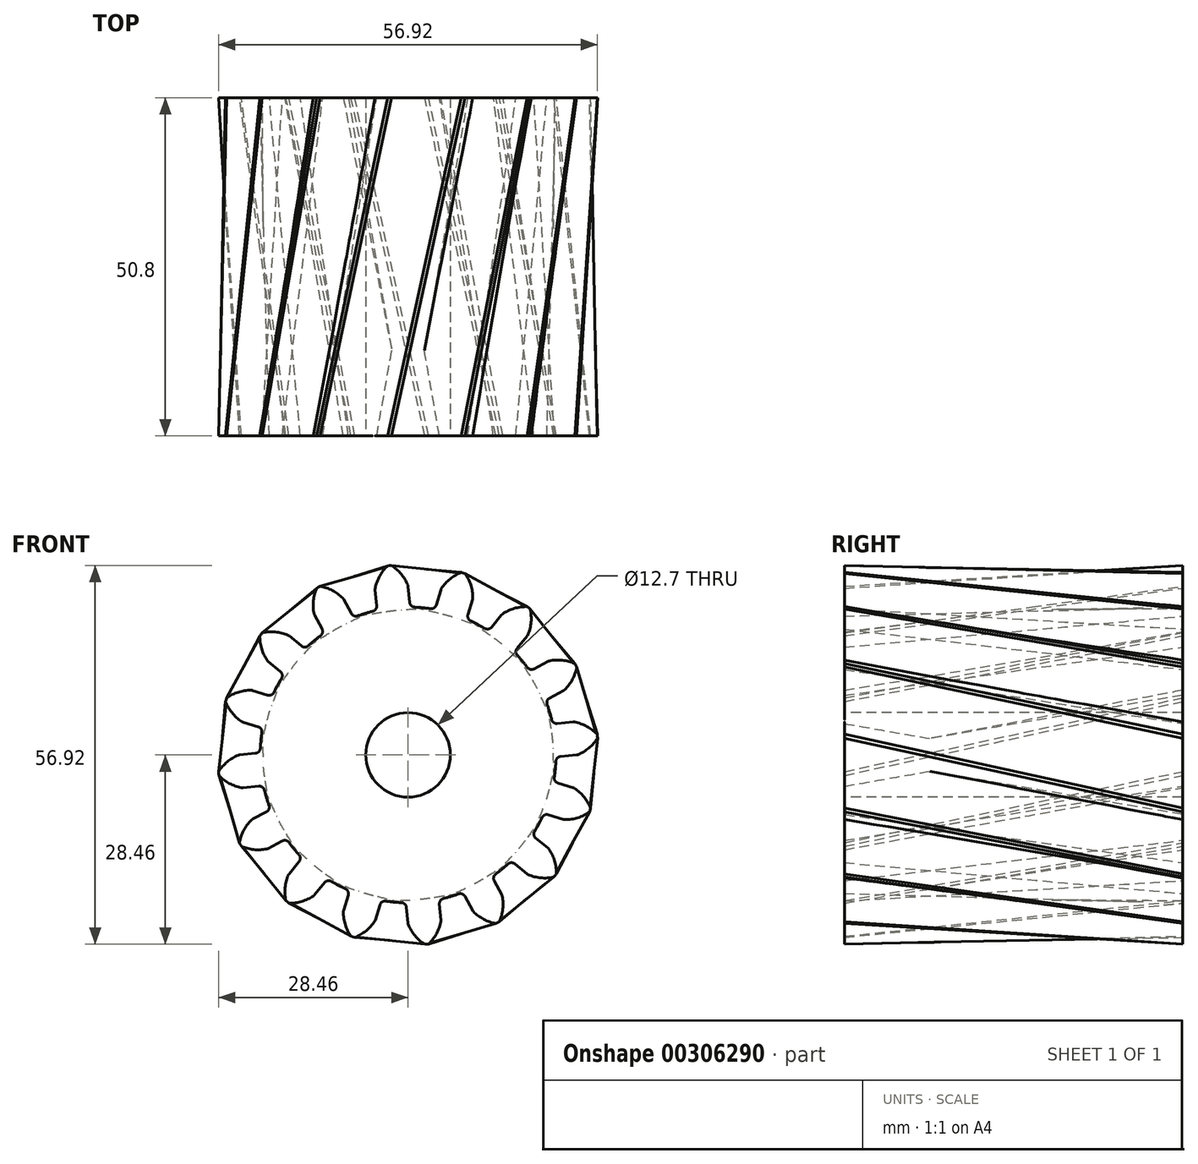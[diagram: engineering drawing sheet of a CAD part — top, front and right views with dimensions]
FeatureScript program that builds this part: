
annotation { "Feature Type Name" : "Feature", "Feature Type Description" : "" }
export const myFeature = defineFeature(function(context is Context, id is Id, definition is map)
    precondition{}
    {
        {
            var Q0;
            Q0=qCreatedBy(makeId("Front.planeOp"),FACE);
            var sketch = newSketch(context, id + "F0", { "sketchPlane" : qUnion([Q0])});
            skArc(sketch, "E0", {"start": v(-5.3, 21.58) * mm, "mid": v(-6.45, 21.27) * mm, "end": v(-7.58, 20.9) * mm});
            skArc(sketch, "E1.trimOffspring", {"start": v(-0.04, 25.51) * mm, "mid": v(-1.05, 27.18) * mm, "end": v(-2.5, 28.46) * mm});
            skLineSegment(sketch, "E2", {"start": v(-2.5, 28.46) * mm, "end": v(-2.8, 28.44) * mm});
            skLineSegment(sketch, "E3", {"start": v(0.01, 25.29) * mm, "end": v(0.25, 22.91) * mm});
            skLineSegment(sketch, "E4.MirrorCS", {"start": v(-3.1, 28.4) * mm, "end": v(-2.8, 28.44) * mm});
            skArc(sketch, "E5.MirrorCS", {"start": v(-4.93, 25.03) * mm, "mid": v(-4.28, 26.86) * mm, "end": v(-3.1, 28.4) * mm});
            skLineSegment(sketch, "E6.MirrorCS", {"start": v(-4.94, 24.8) * mm, "end": v(-4.71, 22.42) * mm});
            skPoint(sketch, "E7.orphan", {"position": v(-4.37, 19) * mm});
            skPoint(sketch, "E8.orphan", {"position": v(0.58, 19.48) * mm});
            skPoint(sketch, "E9.visualSharp", {"position": v(-4.96, 24.91) * mm});
            skArc(sketch, "E9.filletArc", {"start": v(-4.93, 25.03) * mm, "mid": v(-4.95, 24.92) * mm, "end": v(-4.94, 24.8) * mm});
            skPoint(sketch, "E10.visualSharp", {"position": v(0, 25.4) * mm});
            skArc(sketch, "E10.filletArc", {"start": v(0.01, 25.29) * mm, "mid": v(0, 25.4) * mm, "end": v(-0.04, 25.51) * mm});
            skPoint(sketch, "E11.visualSharp", {"position": v(0.31, 22.22) * mm});
            skArc(sketch, "E11.filletArc", {"start": v(0.25, 22.91) * mm, "mid": v(0.49, 22.42) * mm, "end": v(1, 22.2) * mm});
            skPoint(sketch, "E12.visualSharp", {"position": v(-4.64, 21.73) * mm});
            skArc(sketch, "E12.filletArc", {"start": v(-5.3, 21.58) * mm, "mid": v(-4.85, 21.9) * mm, "end": v(-4.71, 22.42) * mm});
            skArc(sketch, "E13.1.0", {"start": v(-14.14, 21.24) * mm, "mid": v(-14.23, 23.18) * mm, "end": v(-13.73, 25.06) * mm});
            skArc(sketch, "E13.1.1", {"start": v(-14.14, 21.24) * mm, "mid": v(-14.1, 21.13) * mm, "end": v(-14.06, 21.02) * mm});
            skLineSegment(sketch, "E13.1.2", {"start": v(-14.06, 21.02) * mm, "end": v(-12.93, 18.91) * mm});
            skArc(sketch, "E13.1.3", {"start": v(-9.67, 23.37) * mm, "mid": v(-9.73, 23.47) * mm, "end": v(-9.8, 23.55) * mm});
            skArc(sketch, "E13.1.4", {"start": v(-9.8, 23.55) * mm, "mid": v(-11.37, 24.7) * mm, "end": v(-13.21, 25.34) * mm});
            skLineSegment(sketch, "E13.1.5", {"start": v(-9.67, 23.37) * mm, "end": v(-8.54, 21.26) * mm});
            skLineSegment(sketch, "E13.1.6", {"start": v(-13.21, 25.34) * mm, "end": v(-13.47, 25.2) * mm});
            skLineSegment(sketch, "E13.1.7", {"start": v(-13.73, 25.06) * mm, "end": v(-13.47, 25.2) * mm});
            skArc(sketch, "E13.1.8", {"start": v(-13.16, 17.9) * mm, "mid": v(-12.86, 18.37) * mm, "end": v(-12.93, 18.91) * mm});
            skArc(sketch, "E13.1.9", {"start": v(-8.54, 21.26) * mm, "mid": v(-8.13, 20.9) * mm, "end": v(-7.58, 20.9) * mm});
            skArc(sketch, "E13.2.0", {"start": v(-21.19, 14.2) * mm, "mid": v(-22.02, 15.97) * mm, "end": v(-22.27, 17.9) * mm});
            skArc(sketch, "E13.2.1", {"start": v(-21.19, 14.2) * mm, "mid": v(-21.12, 14.12) * mm, "end": v(-21.03, 14.04) * mm});
            skLineSegment(sketch, "E13.2.2", {"start": v(-21.03, 14.04) * mm, "end": v(-19.19, 12.53) * mm});
            skArc(sketch, "E13.2.3", {"start": v(-17.87, 17.9) * mm, "mid": v(-17.97, 17.96) * mm, "end": v(-18.07, 18) * mm});
            skArc(sketch, "E13.2.4", {"start": v(-18.07, 18) * mm, "mid": v(-19.96, 18.48) * mm, "end": v(-21.9, 18.35) * mm});
            skLineSegment(sketch, "E13.2.5", {"start": v(-17.87, 17.9) * mm, "end": v(-16.03, 16.37) * mm});
            skLineSegment(sketch, "E13.2.6", {"start": v(-21.9, 18.35) * mm, "end": v(-22.09, 18.13) * mm});
            skLineSegment(sketch, "E13.2.7", {"start": v(-22.27, 17.9) * mm, "end": v(-22.09, 18.13) * mm});
            skArc(sketch, "E13.2.8", {"start": v(-19.01, 11.5) * mm, "mid": v(-18.91, 12.05) * mm, "end": v(-19.19, 12.53) * mm});
            skArc(sketch, "E13.2.9", {"start": v(-16.03, 16.37) * mm, "mid": v(-15.5, 16.2) * mm, "end": v(-15, 16.4) * mm});
            skArc(sketch, "E14.2.3.0", {"start": v(-25.01, 5.02) * mm, "mid": v(-26.45, 6.33) * mm, "end": v(-27.43, 8.01) * mm});
            skArc(sketch, "E14.4.3.0", {"start": v(-25.01, 5.02) * mm, "mid": v(-24.91, 4.96) * mm, "end": v(-24.8, 4.92) * mm});
            skLineSegment(sketch, "E14.8.3.0", {"start": v(-24.8, 4.92) * mm, "end": v(-22.52, 4.23) * mm});
            skArc(sketch, "E14.11.3.0", {"start": v(-23.36, 9.69) * mm, "mid": v(-23.47, 9.71) * mm, "end": v(-23.58, 9.72) * mm});
            skArc(sketch, "E14.15.3.0", {"start": v(-23.58, 9.72) * mm, "mid": v(-25.51, 9.43) * mm, "end": v(-27.26, 8.58) * mm});
            skLineSegment(sketch, "E14.19.3.0", {"start": v(-23.36, 9.69) * mm, "end": v(-21.07, 9) * mm});
            skLineSegment(sketch, "E14.22.3.0", {"start": v(-27.26, 8.58) * mm, "end": v(-27.35, 8.3) * mm});
            skLineSegment(sketch, "E14.25.3.0", {"start": v(-27.43, 8.01) * mm, "end": v(-27.35, 8.3) * mm});
            skArc(sketch, "E14.28.3.0", {"start": v(-21.97, 3.36) * mm, "mid": v(-22.08, 3.9) * mm, "end": v(-22.52, 4.23) * mm});
            skArc(sketch, "E14.32.3.0", {"start": v(-21.07, 9) * mm, "mid": v(-20.53, 9.03) * mm, "end": v(-20.13, 9.41) * mm});
            skArc(sketch, "E14.2.4.0", {"start": v(-25.03, -4.93) * mm, "mid": v(-26.86, -4.28) * mm, "end": v(-28.4, -3.1) * mm});
            skArc(sketch, "E14.4.4.0", {"start": v(-25.03, -4.93) * mm, "mid": v(-24.92, -4.95) * mm, "end": v(-24.8, -4.94) * mm});
            skLineSegment(sketch, "E14.8.4.0", {"start": v(-24.8, -4.94) * mm, "end": v(-22.42, -4.71) * mm});
            skArc(sketch, "E14.11.4.0", {"start": v(-25.29, 0.01) * mm, "mid": v(-25.4, 0) * mm, "end": v(-25.51, -0.04) * mm});
            skArc(sketch, "E14.15.4.0", {"start": v(-25.51, -0.04) * mm, "mid": v(-27.18, -1.05) * mm, "end": v(-28.46, -2.5) * mm});
            skLineSegment(sketch, "E14.19.4.0", {"start": v(-25.29, 0.01) * mm, "end": v(-22.91, 0.25) * mm});
            skLineSegment(sketch, "E14.22.4.0", {"start": v(-28.46, -2.5) * mm, "end": v(-28.44, -2.8) * mm});
            skLineSegment(sketch, "E14.25.4.0", {"start": v(-28.4, -3.1) * mm, "end": v(-28.44, -2.8) * mm});
            skArc(sketch, "E14.28.4.0", {"start": v(-21.58, -5.3) * mm, "mid": v(-21.9, -4.85) * mm, "end": v(-22.42, -4.71) * mm});
            skArc(sketch, "E14.32.4.0", {"start": v(-22.91, 0.25) * mm, "mid": v(-22.42, 0.49) * mm, "end": v(-22.2, 1) * mm});
            skArc(sketch, "E14.2.5.0", {"start": v(-21.24, -14.14) * mm, "mid": v(-23.18, -14.23) * mm, "end": v(-25.06, -13.73) * mm});
            skArc(sketch, "E14.4.5.0", {"start": v(-21.24, -14.14) * mm, "mid": v(-21.13, -14.1) * mm, "end": v(-21.02, -14.06) * mm});
            skLineSegment(sketch, "E14.8.5.0", {"start": v(-21.02, -14.06) * mm, "end": v(-18.91, -12.93) * mm});
            skArc(sketch, "E14.11.5.0", {"start": v(-23.37, -9.67) * mm, "mid": v(-23.47, -9.73) * mm, "end": v(-23.55, -9.8) * mm});
            skArc(sketch, "E14.15.5.0", {"start": v(-23.55, -9.8) * mm, "mid": v(-24.7, -11.37) * mm, "end": v(-25.34, -13.21) * mm});
            skLineSegment(sketch, "E14.19.5.0", {"start": v(-23.37, -9.67) * mm, "end": v(-21.26, -8.54) * mm});
            skLineSegment(sketch, "E14.22.5.0", {"start": v(-25.34, -13.21) * mm, "end": v(-25.2, -13.47) * mm});
            skLineSegment(sketch, "E14.25.5.0", {"start": v(-25.06, -13.73) * mm, "end": v(-25.2, -13.47) * mm});
            skArc(sketch, "E14.28.5.0", {"start": v(-17.9, -13.16) * mm, "mid": v(-18.37, -12.86) * mm, "end": v(-18.91, -12.93) * mm});
            skArc(sketch, "E14.32.5.0", {"start": v(-21.26, -8.54) * mm, "mid": v(-20.9, -8.13) * mm, "end": v(-20.9, -7.58) * mm});
            skArc(sketch, "E14.2.6.0", {"start": v(-14.2, -21.19) * mm, "mid": v(-15.97, -22.02) * mm, "end": v(-17.9, -22.27) * mm});
            skArc(sketch, "E14.4.6.0", {"start": v(-14.2, -21.19) * mm, "mid": v(-14.12, -21.12) * mm, "end": v(-14.04, -21.03) * mm});
            skLineSegment(sketch, "E14.8.6.0", {"start": v(-14.04, -21.03) * mm, "end": v(-12.53, -19.19) * mm});
            skArc(sketch, "E14.11.6.0", {"start": v(-17.9, -17.87) * mm, "mid": v(-17.96, -17.97) * mm, "end": v(-18, -18.07) * mm});
            skArc(sketch, "E14.15.6.0", {"start": v(-18, -18.07) * mm, "mid": v(-18.48, -19.96) * mm, "end": v(-18.35, -21.9) * mm});
            skLineSegment(sketch, "E14.19.6.0", {"start": v(-17.9, -17.87) * mm, "end": v(-16.37, -16.03) * mm});
            skLineSegment(sketch, "E14.22.6.0", {"start": v(-18.35, -21.9) * mm, "end": v(-18.13, -22.09) * mm});
            skLineSegment(sketch, "E14.25.6.0", {"start": v(-17.9, -22.27) * mm, "end": v(-18.13, -22.09) * mm});
            skArc(sketch, "E14.28.6.0", {"start": v(-11.5, -19.01) * mm, "mid": v(-12.05, -18.91) * mm, "end": v(-12.53, -19.19) * mm});
            skArc(sketch, "E14.32.6.0", {"start": v(-16.37, -16.03) * mm, "mid": v(-16.2, -15.5) * mm, "end": v(-16.4, -15) * mm});
            skArc(sketch, "E14.2.7.0", {"start": v(-5.02, -25.01) * mm, "mid": v(-6.33, -26.45) * mm, "end": v(-8.01, -27.43) * mm});
            skArc(sketch, "E14.4.7.0", {"start": v(-5.02, -25.01) * mm, "mid": v(-4.96, -24.91) * mm, "end": v(-4.92, -24.8) * mm});
            skLineSegment(sketch, "E14.8.7.0", {"start": v(-4.92, -24.8) * mm, "end": v(-4.23, -22.52) * mm});
            skArc(sketch, "E14.11.7.0", {"start": v(-9.69, -23.36) * mm, "mid": v(-9.71, -23.47) * mm, "end": v(-9.72, -23.58) * mm});
            skArc(sketch, "E14.15.7.0", {"start": v(-9.72, -23.58) * mm, "mid": v(-9.43, -25.51) * mm, "end": v(-8.58, -27.26) * mm});
            skLineSegment(sketch, "E14.19.7.0", {"start": v(-9.69, -23.36) * mm, "end": v(-9, -21.07) * mm});
            skLineSegment(sketch, "E14.22.7.0", {"start": v(-8.58, -27.26) * mm, "end": v(-8.3, -27.35) * mm});
            skLineSegment(sketch, "E14.25.7.0", {"start": v(-8.01, -27.43) * mm, "end": v(-8.3, -27.35) * mm});
            skArc(sketch, "E14.28.7.0", {"start": v(-3.36, -21.97) * mm, "mid": v(-3.9, -22.08) * mm, "end": v(-4.23, -22.52) * mm});
            skArc(sketch, "E14.32.7.0", {"start": v(-9, -21.07) * mm, "mid": v(-9.03, -20.53) * mm, "end": v(-9.41, -20.13) * mm});
            skArc(sketch, "E14.2.8.0", {"start": v(4.93, -25.03) * mm, "mid": v(4.28, -26.86) * mm, "end": v(3.1, -28.4) * mm});
            skArc(sketch, "E14.4.8.0", {"start": v(4.93, -25.03) * mm, "mid": v(4.95, -24.92) * mm, "end": v(4.94, -24.8) * mm});
            skLineSegment(sketch, "E14.8.8.0", {"start": v(4.94, -24.8) * mm, "end": v(4.71, -22.42) * mm});
            skArc(sketch, "E14.11.8.0", {"start": v(-0.01, -25.29) * mm, "mid": v(0, -25.4) * mm, "end": v(0.04, -25.51) * mm});
            skArc(sketch, "E14.15.8.0", {"start": v(0.04, -25.51) * mm, "mid": v(1.05, -27.18) * mm, "end": v(2.5, -28.46) * mm});
            skLineSegment(sketch, "E14.19.8.0", {"start": v(-0.01, -25.29) * mm, "end": v(-0.25, -22.91) * mm});
            skLineSegment(sketch, "E14.22.8.0", {"start": v(2.5, -28.46) * mm, "end": v(2.8, -28.44) * mm});
            skLineSegment(sketch, "E14.25.8.0", {"start": v(3.1, -28.4) * mm, "end": v(2.8, -28.44) * mm});
            skArc(sketch, "E14.28.8.0", {"start": v(5.3, -21.58) * mm, "mid": v(4.85, -21.9) * mm, "end": v(4.71, -22.42) * mm});
            skArc(sketch, "E14.32.8.0", {"start": v(-0.25, -22.91) * mm, "mid": v(-0.49, -22.42) * mm, "end": v(-1, -22.2) * mm});
            skArc(sketch, "E14.2.9.0", {"start": v(14.14, -21.24) * mm, "mid": v(14.23, -23.18) * mm, "end": v(13.73, -25.06) * mm});
            skArc(sketch, "E14.4.9.0", {"start": v(14.14, -21.24) * mm, "mid": v(14.1, -21.13) * mm, "end": v(14.06, -21.02) * mm});
            skLineSegment(sketch, "E14.8.9.0", {"start": v(14.06, -21.02) * mm, "end": v(12.93, -18.91) * mm});
            skArc(sketch, "E14.11.9.0", {"start": v(9.67, -23.37) * mm, "mid": v(9.73, -23.47) * mm, "end": v(9.8, -23.55) * mm});
            skArc(sketch, "E14.15.9.0", {"start": v(9.8, -23.55) * mm, "mid": v(11.37, -24.7) * mm, "end": v(13.21, -25.34) * mm});
            skLineSegment(sketch, "E14.19.9.0", {"start": v(9.67, -23.37) * mm, "end": v(8.54, -21.26) * mm});
            skLineSegment(sketch, "E14.22.9.0", {"start": v(13.21, -25.34) * mm, "end": v(13.47, -25.2) * mm});
            skLineSegment(sketch, "E14.25.9.0", {"start": v(13.73, -25.06) * mm, "end": v(13.47, -25.2) * mm});
            skArc(sketch, "E14.28.9.0", {"start": v(13.16, -17.9) * mm, "mid": v(12.86, -18.37) * mm, "end": v(12.93, -18.91) * mm});
            skArc(sketch, "E14.32.9.0", {"start": v(8.54, -21.26) * mm, "mid": v(8.13, -20.9) * mm, "end": v(7.58, -20.9) * mm});
            skArc(sketch, "E14.2.10.0", {"start": v(21.19, -14.2) * mm, "mid": v(22.02, -15.97) * mm, "end": v(22.27, -17.9) * mm});
            skArc(sketch, "E14.4.10.0", {"start": v(21.19, -14.2) * mm, "mid": v(21.12, -14.12) * mm, "end": v(21.03, -14.04) * mm});
            skLineSegment(sketch, "E14.8.10.0", {"start": v(21.03, -14.04) * mm, "end": v(19.19, -12.53) * mm});
            skArc(sketch, "E14.11.10.0", {"start": v(17.87, -17.9) * mm, "mid": v(17.97, -17.96) * mm, "end": v(18.07, -18) * mm});
            skArc(sketch, "E14.15.10.0", {"start": v(18.07, -18) * mm, "mid": v(19.96, -18.48) * mm, "end": v(21.9, -18.35) * mm});
            skLineSegment(sketch, "E14.19.10.0", {"start": v(17.87, -17.9) * mm, "end": v(16.03, -16.37) * mm});
            skLineSegment(sketch, "E14.22.10.0", {"start": v(21.9, -18.35) * mm, "end": v(22.09, -18.13) * mm});
            skLineSegment(sketch, "E14.25.10.0", {"start": v(22.27, -17.9) * mm, "end": v(22.09, -18.13) * mm});
            skArc(sketch, "E14.28.10.0", {"start": v(19.01, -11.5) * mm, "mid": v(18.91, -12.05) * mm, "end": v(19.19, -12.53) * mm});
            skArc(sketch, "E14.32.10.0", {"start": v(16.03, -16.37) * mm, "mid": v(15.5, -16.2) * mm, "end": v(15, -16.4) * mm});
            skArc(sketch, "E14.2.11.0", {"start": v(25.01, -5.02) * mm, "mid": v(26.45, -6.33) * mm, "end": v(27.43, -8.01) * mm});
            skArc(sketch, "E14.4.11.0", {"start": v(25.01, -5.02) * mm, "mid": v(24.91, -4.96) * mm, "end": v(24.8, -4.92) * mm});
            skLineSegment(sketch, "E14.8.11.0", {"start": v(24.8, -4.92) * mm, "end": v(22.52, -4.23) * mm});
            skArc(sketch, "E14.11.11.0", {"start": v(23.36, -9.69) * mm, "mid": v(23.47, -9.71) * mm, "end": v(23.58, -9.72) * mm});
            skArc(sketch, "E14.15.11.0", {"start": v(23.58, -9.72) * mm, "mid": v(25.51, -9.43) * mm, "end": v(27.26, -8.58) * mm});
            skLineSegment(sketch, "E14.19.11.0", {"start": v(23.36, -9.69) * mm, "end": v(21.07, -9) * mm});
            skLineSegment(sketch, "E14.22.11.0", {"start": v(27.26, -8.58) * mm, "end": v(27.35, -8.3) * mm});
            skLineSegment(sketch, "E14.25.11.0", {"start": v(27.43, -8.01) * mm, "end": v(27.35, -8.3) * mm});
            skArc(sketch, "E14.28.11.0", {"start": v(21.97, -3.36) * mm, "mid": v(22.08, -3.9) * mm, "end": v(22.52, -4.23) * mm});
            skArc(sketch, "E14.32.11.0", {"start": v(21.07, -9) * mm, "mid": v(20.53, -9.03) * mm, "end": v(20.13, -9.41) * mm});
            skArc(sketch, "E14.2.12.0", {"start": v(25.03, 4.93) * mm, "mid": v(26.86, 4.28) * mm, "end": v(28.4, 3.1) * mm});
            skArc(sketch, "E14.4.12.0", {"start": v(25.03, 4.93) * mm, "mid": v(24.92, 4.95) * mm, "end": v(24.8, 4.94) * mm});
            skLineSegment(sketch, "E14.8.12.0", {"start": v(24.8, 4.94) * mm, "end": v(22.42, 4.71) * mm});
            skArc(sketch, "E14.11.12.0", {"start": v(25.29, -0.01) * mm, "mid": v(25.4, 0) * mm, "end": v(25.51, 0.04) * mm});
            skArc(sketch, "E14.15.12.0", {"start": v(25.51, 0.04) * mm, "mid": v(27.18, 1.05) * mm, "end": v(28.46, 2.5) * mm});
            skLineSegment(sketch, "E14.19.12.0", {"start": v(25.29, -0.01) * mm, "end": v(22.91, -0.25) * mm});
            skLineSegment(sketch, "E14.22.12.0", {"start": v(28.46, 2.5) * mm, "end": v(28.44, 2.8) * mm});
            skLineSegment(sketch, "E14.25.12.0", {"start": v(28.4, 3.1) * mm, "end": v(28.44, 2.8) * mm});
            skArc(sketch, "E14.28.12.0", {"start": v(21.58, 5.3) * mm, "mid": v(21.9, 4.85) * mm, "end": v(22.42, 4.71) * mm});
            skArc(sketch, "E14.32.12.0", {"start": v(22.91, -0.25) * mm, "mid": v(22.42, -0.49) * mm, "end": v(22.2, -1) * mm});
            skArc(sketch, "E14.2.13.0", {"start": v(21.24, 14.14) * mm, "mid": v(23.18, 14.23) * mm, "end": v(25.06, 13.73) * mm});
            skArc(sketch, "E14.4.13.0", {"start": v(21.24, 14.14) * mm, "mid": v(21.13, 14.1) * mm, "end": v(21.02, 14.06) * mm});
            skLineSegment(sketch, "E14.8.13.0", {"start": v(21.02, 14.06) * mm, "end": v(18.91, 12.93) * mm});
            skArc(sketch, "E14.11.13.0", {"start": v(23.37, 9.67) * mm, "mid": v(23.47, 9.73) * mm, "end": v(23.55, 9.8) * mm});
            skArc(sketch, "E14.15.13.0", {"start": v(23.55, 9.8) * mm, "mid": v(24.7, 11.37) * mm, "end": v(25.34, 13.21) * mm});
            skLineSegment(sketch, "E14.19.13.0", {"start": v(23.37, 9.67) * mm, "end": v(21.26, 8.54) * mm});
            skLineSegment(sketch, "E14.22.13.0", {"start": v(25.34, 13.21) * mm, "end": v(25.2, 13.47) * mm});
            skLineSegment(sketch, "E14.25.13.0", {"start": v(25.06, 13.73) * mm, "end": v(25.2, 13.47) * mm});
            skArc(sketch, "E14.28.13.0", {"start": v(17.9, 13.16) * mm, "mid": v(18.37, 12.86) * mm, "end": v(18.91, 12.93) * mm});
            skArc(sketch, "E14.32.13.0", {"start": v(21.26, 8.54) * mm, "mid": v(20.9, 8.13) * mm, "end": v(20.9, 7.58) * mm});
            skArc(sketch, "E14.2.14.0", {"start": v(14.2, 21.19) * mm, "mid": v(15.97, 22.02) * mm, "end": v(17.9, 22.27) * mm});
            skArc(sketch, "E14.4.14.0", {"start": v(14.2, 21.19) * mm, "mid": v(14.12, 21.12) * mm, "end": v(14.04, 21.03) * mm});
            skLineSegment(sketch, "E14.8.14.0", {"start": v(14.04, 21.03) * mm, "end": v(12.53, 19.19) * mm});
            skArc(sketch, "E14.11.14.0", {"start": v(17.9, 17.87) * mm, "mid": v(17.96, 17.97) * mm, "end": v(18, 18.07) * mm});
            skArc(sketch, "E14.15.14.0", {"start": v(18, 18.07) * mm, "mid": v(18.48, 19.96) * mm, "end": v(18.35, 21.9) * mm});
            skLineSegment(sketch, "E14.19.14.0", {"start": v(17.9, 17.87) * mm, "end": v(16.37, 16.03) * mm});
            skLineSegment(sketch, "E14.22.14.0", {"start": v(18.35, 21.9) * mm, "end": v(18.13, 22.09) * mm});
            skLineSegment(sketch, "E14.25.14.0", {"start": v(17.9, 22.27) * mm, "end": v(18.13, 22.09) * mm});
            skArc(sketch, "E14.28.14.0", {"start": v(11.5, 19.01) * mm, "mid": v(12.05, 18.91) * mm, "end": v(12.53, 19.19) * mm});
            skArc(sketch, "E14.32.14.0", {"start": v(16.37, 16.03) * mm, "mid": v(16.2, 15.5) * mm, "end": v(16.4, 15) * mm});
            skArc(sketch, "E14.2.15.0", {"start": v(5.02, 25.01) * mm, "mid": v(6.33, 26.45) * mm, "end": v(8.01, 27.43) * mm});
            skArc(sketch, "E14.4.15.0", {"start": v(5.02, 25.01) * mm, "mid": v(4.96, 24.91) * mm, "end": v(4.92, 24.8) * mm});
            skLineSegment(sketch, "E14.8.15.0", {"start": v(4.92, 24.8) * mm, "end": v(4.23, 22.52) * mm});
            skArc(sketch, "E14.11.15.0", {"start": v(9.69, 23.36) * mm, "mid": v(9.71, 23.47) * mm, "end": v(9.72, 23.58) * mm});
            skArc(sketch, "E14.15.15.0", {"start": v(9.72, 23.58) * mm, "mid": v(9.43, 25.51) * mm, "end": v(8.58, 27.26) * mm});
            skLineSegment(sketch, "E14.19.15.0", {"start": v(9.69, 23.36) * mm, "end": v(9, 21.07) * mm});
            skLineSegment(sketch, "E14.22.15.0", {"start": v(8.58, 27.26) * mm, "end": v(8.3, 27.35) * mm});
            skLineSegment(sketch, "E14.25.15.0", {"start": v(8.01, 27.43) * mm, "end": v(8.3, 27.35) * mm});
            skArc(sketch, "E14.28.15.0", {"start": v(3.36, 21.97) * mm, "mid": v(3.9, 22.08) * mm, "end": v(4.23, 22.52) * mm});
            skArc(sketch, "E14.32.15.0", {"start": v(9, 21.07) * mm, "mid": v(9.03, 20.53) * mm, "end": v(9.41, 20.13) * mm});
            skArc(sketch, "E15.trimOffspring", {"start": v(-13.16, 17.9) * mm, "mid": v(-14.1, 17.18) * mm, "end": v(-15, 16.4) * mm});
            skArc(sketch, "E16.trimOffspring", {"start": v(-19.01, 11.5) * mm, "mid": v(-19.6, 10.48) * mm, "end": v(-20.13, 9.41) * mm});
            skArc(sketch, "E17.trimOffspring", {"start": v(-21.97, 3.36) * mm, "mid": v(-22.12, 2.18) * mm, "end": v(-22.2, 1) * mm});
            skArc(sketch, "E18.trimOffspring", {"start": v(-21.58, -5.3) * mm, "mid": v(-21.27, -6.45) * mm, "end": v(-20.9, -7.58) * mm});
            skArc(sketch, "E19.trimOffspring", {"start": v(-17.9, -13.16) * mm, "mid": v(-17.18, -14.1) * mm, "end": v(-16.4, -15) * mm});
            skArc(sketch, "E20.trimOffspring", {"start": v(-11.5, -19.01) * mm, "mid": v(-10.48, -19.6) * mm, "end": v(-9.41, -20.13) * mm});
            skArc(sketch, "E21.trimOffspring", {"start": v(-3.36, -21.97) * mm, "mid": v(-2.18, -22.12) * mm, "end": v(-1, -22.2) * mm});
            skArc(sketch, "E22.trimOffspring", {"start": v(5.3, -21.58) * mm, "mid": v(6.45, -21.27) * mm, "end": v(7.58, -20.9) * mm});
            skArc(sketch, "E23.trimOffspring", {"start": v(13.16, -17.9) * mm, "mid": v(14.1, -17.18) * mm, "end": v(15, -16.4) * mm});
            skArc(sketch, "E24.trimOffspring", {"start": v(19.01, -11.5) * mm, "mid": v(19.6, -10.48) * mm, "end": v(20.13, -9.41) * mm});
            skArc(sketch, "E25.trimOffspring", {"start": v(21.97, -3.36) * mm, "mid": v(22.12, -2.18) * mm, "end": v(22.2, -1) * mm});
            skArc(sketch, "E26.trimOffspring", {"start": v(21.58, 5.3) * mm, "mid": v(21.27, 6.45) * mm, "end": v(20.9, 7.58) * mm});
            skArc(sketch, "E27.trimOffspring", {"start": v(17.9, 13.16) * mm, "mid": v(17.18, 14.1) * mm, "end": v(16.4, 15) * mm});
            skArc(sketch, "E28.trimOffspring", {"start": v(11.5, 19.01) * mm, "mid": v(10.48, 19.6) * mm, "end": v(9.41, 20.13) * mm});
            skArc(sketch, "E29.trimOffspring", {"start": v(3.36, 21.97) * mm, "mid": v(2.18, 22.12) * mm, "end": v(1, 22.2) * mm});
            skSolve(sketch);
        }
        {
            var Q0;
            Q0=makeQuery(id+"F0.imprint","IMPRINT",FACE,{"disambiguationData":[TD([[makeQuery(id+"F0.imprint","IMPRINT",EDGE,{"derivedFrom":sQuery(id+"F0.wireOp",EDGE,"E0")}),1.0]])]});
            cPlane(context, id + "F1", {"entities" : qUnion([Q0]), "cplaneType" : CPlaneType.OFFSET, "offset" : 50.8 * mm, "width" : 152.4 * mm, "height" : 152.4 * mm});
        }
        {
            var Q0;
            Q0=qCreatedBy(id+"F1.planeOp",FACE);
            var sketch = newSketch(context, id + "F2", { "sketchPlane" : qUnion([Q0])});
            skLineSegment(sketch, "E30.0.0", {"start": v(8.54, -21.26) * mm, "end": v(9.67, -23.37) * mm});
            skArc(sketch, "E30.0.1", {"start": v(9.67, -23.37) * mm, "mid": v(9.73, -23.47) * mm, "end": v(9.8, -23.55) * mm});
            skArc(sketch, "E30.0.2", {"start": v(9.8, -23.55) * mm, "mid": v(11.37, -24.7) * mm, "end": v(13.21, -25.34) * mm});
            skLineSegment(sketch, "E30.0.3", {"start": v(13.21, -25.34) * mm, "end": v(13.47, -25.2) * mm});
            skLineSegment(sketch, "E30.0.4", {"start": v(13.47, -25.2) * mm, "end": v(13.73, -25.06) * mm});
            skArc(sketch, "E30.0.5", {"start": v(13.73, -25.06) * mm, "mid": v(14.23, -23.18) * mm, "end": v(14.14, -21.24) * mm});
            skArc(sketch, "E30.0.6", {"start": v(14.14, -21.24) * mm, "mid": v(14.1, -21.13) * mm, "end": v(14.06, -21.02) * mm});
            skLineSegment(sketch, "E30.0.7", {"start": v(14.06, -21.02) * mm, "end": v(12.93, -18.91) * mm});
            skArc(sketch, "E30.0.8", {"start": v(12.93, -18.91) * mm, "mid": v(12.86, -18.37) * mm, "end": v(13.16, -17.9) * mm});
            skArc(sketch, "E30.0.9", {"start": v(13.16, -17.9) * mm, "mid": v(14.1, -17.18) * mm, "end": v(15, -16.4) * mm});
            skArc(sketch, "E30.0.10", {"start": v(15, -16.4) * mm, "mid": v(15.5, -16.2) * mm, "end": v(16.03, -16.37) * mm});
            skLineSegment(sketch, "E30.0.11", {"start": v(16.03, -16.37) * mm, "end": v(17.87, -17.9) * mm});
            skArc(sketch, "E30.0.12", {"start": v(17.87, -17.9) * mm, "mid": v(17.97, -17.96) * mm, "end": v(18.07, -18) * mm});
            skArc(sketch, "E30.0.13", {"start": v(18.07, -18) * mm, "mid": v(19.96, -18.48) * mm, "end": v(21.9, -18.35) * mm});
            skLineSegment(sketch, "E30.0.14", {"start": v(21.9, -18.35) * mm, "end": v(22.09, -18.13) * mm});
            skLineSegment(sketch, "E30.0.15", {"start": v(22.09, -18.13) * mm, "end": v(22.27, -17.9) * mm});
            skArc(sketch, "E30.0.16", {"start": v(22.27, -17.9) * mm, "mid": v(22.02, -15.97) * mm, "end": v(21.19, -14.2) * mm});
            skArc(sketch, "E30.0.17", {"start": v(21.19, -14.2) * mm, "mid": v(21.12, -14.12) * mm, "end": v(21.03, -14.04) * mm});
            skLineSegment(sketch, "E30.0.18", {"start": v(21.03, -14.04) * mm, "end": v(19.19, -12.53) * mm});
            skArc(sketch, "E30.0.19", {"start": v(19.19, -12.53) * mm, "mid": v(18.91, -12.05) * mm, "end": v(19.01, -11.5) * mm});
            skArc(sketch, "E30.0.20", {"start": v(19.01, -11.5) * mm, "mid": v(19.6, -10.48) * mm, "end": v(20.13, -9.41) * mm});
            skArc(sketch, "E30.0.21", {"start": v(20.13, -9.41) * mm, "mid": v(20.53, -9.03) * mm, "end": v(21.07, -9) * mm});
            skLineSegment(sketch, "E30.0.22", {"start": v(21.07, -9) * mm, "end": v(23.36, -9.69) * mm});
            skArc(sketch, "E30.0.23", {"start": v(23.36, -9.69) * mm, "mid": v(23.47, -9.71) * mm, "end": v(23.58, -9.72) * mm});
            skArc(sketch, "E30.0.24", {"start": v(23.58, -9.72) * mm, "mid": v(25.51, -9.43) * mm, "end": v(27.26, -8.58) * mm});
            skLineSegment(sketch, "E30.0.25", {"start": v(27.26, -8.58) * mm, "end": v(27.35, -8.3) * mm});
            skLineSegment(sketch, "E30.0.26", {"start": v(27.35, -8.3) * mm, "end": v(27.43, -8.01) * mm});
            skArc(sketch, "E30.0.27", {"start": v(27.43, -8.01) * mm, "mid": v(26.45, -6.33) * mm, "end": v(25.01, -5.02) * mm});
            skArc(sketch, "E30.0.28", {"start": v(25.01, -5.02) * mm, "mid": v(24.91, -4.96) * mm, "end": v(24.8, -4.92) * mm});
            skLineSegment(sketch, "E30.0.29", {"start": v(24.8, -4.92) * mm, "end": v(22.52, -4.23) * mm});
            skArc(sketch, "E30.0.30", {"start": v(22.52, -4.23) * mm, "mid": v(22.08, -3.9) * mm, "end": v(21.97, -3.36) * mm});
            skArc(sketch, "E30.0.31", {"start": v(21.97, -3.36) * mm, "mid": v(22.12, -2.18) * mm, "end": v(22.2, -1) * mm});
            skArc(sketch, "E30.0.32", {"start": v(22.2, -1) * mm, "mid": v(22.42, -0.49) * mm, "end": v(22.91, -0.25) * mm});
            skLineSegment(sketch, "E30.0.33", {"start": v(22.91, -0.25) * mm, "end": v(25.29, -0.01) * mm});
            skArc(sketch, "E30.0.34", {"start": v(25.29, -0.01) * mm, "mid": v(25.4, 0) * mm, "end": v(25.51, 0.04) * mm});
            skArc(sketch, "E30.0.35", {"start": v(25.51, 0.04) * mm, "mid": v(27.18, 1.05) * mm, "end": v(28.46, 2.5) * mm});
            skLineSegment(sketch, "E30.0.36", {"start": v(28.46, 2.5) * mm, "end": v(28.44, 2.8) * mm});
            skLineSegment(sketch, "E30.0.37", {"start": v(28.44, 2.8) * mm, "end": v(28.4, 3.1) * mm});
            skArc(sketch, "E30.0.38", {"start": v(28.4, 3.1) * mm, "mid": v(26.86, 4.28) * mm, "end": v(25.03, 4.93) * mm});
            skArc(sketch, "E30.0.39", {"start": v(25.03, 4.93) * mm, "mid": v(24.92, 4.95) * mm, "end": v(24.8, 4.94) * mm});
            skLineSegment(sketch, "E30.0.40", {"start": v(24.8, 4.94) * mm, "end": v(22.42, 4.71) * mm});
            skArc(sketch, "E30.0.41", {"start": v(22.42, 4.71) * mm, "mid": v(21.9, 4.85) * mm, "end": v(21.58, 5.3) * mm});
            skArc(sketch, "E30.0.42", {"start": v(21.58, 5.3) * mm, "mid": v(21.27, 6.45) * mm, "end": v(20.9, 7.58) * mm});
            skArc(sketch, "E30.0.43", {"start": v(20.9, 7.58) * mm, "mid": v(20.9, 8.13) * mm, "end": v(21.26, 8.54) * mm});
            skLineSegment(sketch, "E30.0.44", {"start": v(21.26, 8.54) * mm, "end": v(23.37, 9.67) * mm});
            skArc(sketch, "E30.0.45", {"start": v(23.37, 9.67) * mm, "mid": v(23.47, 9.73) * mm, "end": v(23.55, 9.8) * mm});
            skArc(sketch, "E30.0.46", {"start": v(23.55, 9.8) * mm, "mid": v(24.7, 11.37) * mm, "end": v(25.34, 13.21) * mm});
            skLineSegment(sketch, "E30.0.47", {"start": v(25.34, 13.21) * mm, "end": v(25.2, 13.47) * mm});
            skLineSegment(sketch, "E30.0.48", {"start": v(25.2, 13.47) * mm, "end": v(25.06, 13.73) * mm});
            skArc(sketch, "E30.0.49", {"start": v(25.06, 13.73) * mm, "mid": v(23.18, 14.23) * mm, "end": v(21.24, 14.14) * mm});
            skArc(sketch, "E30.0.50", {"start": v(21.24, 14.14) * mm, "mid": v(21.13, 14.1) * mm, "end": v(21.02, 14.06) * mm});
            skLineSegment(sketch, "E30.0.51", {"start": v(21.02, 14.06) * mm, "end": v(18.91, 12.93) * mm});
            skArc(sketch, "E30.0.52", {"start": v(18.91, 12.93) * mm, "mid": v(18.37, 12.86) * mm, "end": v(17.9, 13.16) * mm});
            skArc(sketch, "E30.0.53", {"start": v(17.9, 13.16) * mm, "mid": v(17.18, 14.1) * mm, "end": v(16.4, 15) * mm});
            skArc(sketch, "E30.0.54", {"start": v(16.4, 15) * mm, "mid": v(16.2, 15.5) * mm, "end": v(16.37, 16.03) * mm});
            skLineSegment(sketch, "E30.0.55", {"start": v(16.37, 16.03) * mm, "end": v(17.9, 17.87) * mm});
            skArc(sketch, "E30.0.56", {"start": v(17.9, 17.87) * mm, "mid": v(17.96, 17.97) * mm, "end": v(18, 18.07) * mm});
            skArc(sketch, "E30.0.57", {"start": v(18, 18.07) * mm, "mid": v(18.48, 19.96) * mm, "end": v(18.35, 21.9) * mm});
            skLineSegment(sketch, "E30.0.58", {"start": v(18.35, 21.9) * mm, "end": v(18.13, 22.09) * mm});
            skLineSegment(sketch, "E30.0.59", {"start": v(18.13, 22.09) * mm, "end": v(17.9, 22.27) * mm});
            skArc(sketch, "E30.0.60", {"start": v(17.9, 22.27) * mm, "mid": v(15.97, 22.02) * mm, "end": v(14.2, 21.19) * mm});
            skArc(sketch, "E30.0.61", {"start": v(14.2, 21.19) * mm, "mid": v(14.12, 21.12) * mm, "end": v(14.04, 21.03) * mm});
            skLineSegment(sketch, "E30.0.62", {"start": v(14.04, 21.03) * mm, "end": v(12.53, 19.19) * mm});
            skArc(sketch, "E30.0.63", {"start": v(12.53, 19.19) * mm, "mid": v(12.05, 18.91) * mm, "end": v(11.5, 19.01) * mm});
            skArc(sketch, "E30.0.64", {"start": v(11.5, 19.01) * mm, "mid": v(10.48, 19.6) * mm, "end": v(9.41, 20.13) * mm});
            skArc(sketch, "E30.0.65", {"start": v(9.41, 20.13) * mm, "mid": v(9.03, 20.53) * mm, "end": v(9, 21.07) * mm});
            skLineSegment(sketch, "E30.0.66", {"start": v(9, 21.07) * mm, "end": v(9.69, 23.36) * mm});
            skArc(sketch, "E30.0.67", {"start": v(9.69, 23.36) * mm, "mid": v(9.71, 23.47) * mm, "end": v(9.72, 23.58) * mm});
            skArc(sketch, "E30.0.68", {"start": v(9.72, 23.58) * mm, "mid": v(9.43, 25.51) * mm, "end": v(8.58, 27.26) * mm});
            skLineSegment(sketch, "E30.0.69", {"start": v(8.58, 27.26) * mm, "end": v(8.3, 27.35) * mm});
            skLineSegment(sketch, "E30.0.70", {"start": v(8.3, 27.35) * mm, "end": v(8.01, 27.43) * mm});
            skArc(sketch, "E30.0.71", {"start": v(8.01, 27.43) * mm, "mid": v(6.33, 26.45) * mm, "end": v(5.02, 25.01) * mm});
            skArc(sketch, "E30.0.72", {"start": v(5.02, 25.01) * mm, "mid": v(4.96, 24.91) * mm, "end": v(4.92, 24.8) * mm});
            skLineSegment(sketch, "E30.0.73", {"start": v(4.92, 24.8) * mm, "end": v(4.23, 22.52) * mm});
            skArc(sketch, "E30.0.74", {"start": v(4.23, 22.52) * mm, "mid": v(3.9, 22.08) * mm, "end": v(3.36, 21.97) * mm});
            skArc(sketch, "E30.0.75", {"start": v(3.36, 21.97) * mm, "mid": v(2.18, 22.12) * mm, "end": v(1, 22.2) * mm});
            skArc(sketch, "E30.0.76", {"start": v(1, 22.2) * mm, "mid": v(0.49, 22.42) * mm, "end": v(0.25, 22.91) * mm});
            skLineSegment(sketch, "E30.0.77", {"start": v(0.25, 22.91) * mm, "end": v(0.01, 25.29) * mm});
            skArc(sketch, "E30.0.78", {"start": v(0.01, 25.29) * mm, "mid": v(0, 25.4) * mm, "end": v(-0.04, 25.51) * mm});
            skArc(sketch, "E30.0.79", {"start": v(-0.04, 25.51) * mm, "mid": v(-1.05, 27.18) * mm, "end": v(-2.5, 28.46) * mm});
            skLineSegment(sketch, "E30.0.80", {"start": v(-2.5, 28.46) * mm, "end": v(-2.8, 28.44) * mm});
            skLineSegment(sketch, "E30.0.81", {"start": v(-2.8, 28.44) * mm, "end": v(-3.1, 28.4) * mm});
            skArc(sketch, "E30.0.82", {"start": v(-3.1, 28.4) * mm, "mid": v(-4.28, 26.86) * mm, "end": v(-4.93, 25.03) * mm});
            skArc(sketch, "E30.0.83", {"start": v(-4.93, 25.03) * mm, "mid": v(-4.95, 24.92) * mm, "end": v(-4.94, 24.8) * mm});
            skLineSegment(sketch, "E30.0.84", {"start": v(-4.94, 24.8) * mm, "end": v(-4.71, 22.42) * mm});
            skArc(sketch, "E30.0.85", {"start": v(-4.71, 22.42) * mm, "mid": v(-4.85, 21.9) * mm, "end": v(-5.3, 21.58) * mm});
            skArc(sketch, "E30.0.86", {"start": v(-5.3, 21.58) * mm, "mid": v(-6.45, 21.27) * mm, "end": v(-7.58, 20.9) * mm});
            skArc(sketch, "E30.0.87", {"start": v(-7.58, 20.9) * mm, "mid": v(-8.13, 20.9) * mm, "end": v(-8.54, 21.26) * mm});
            skLineSegment(sketch, "E30.0.88", {"start": v(-8.54, 21.26) * mm, "end": v(-9.67, 23.37) * mm});
            skArc(sketch, "E30.0.89", {"start": v(-9.67, 23.37) * mm, "mid": v(-9.73, 23.47) * mm, "end": v(-9.8, 23.55) * mm});
            skArc(sketch, "E30.0.90", {"start": v(-9.8, 23.55) * mm, "mid": v(-11.37, 24.7) * mm, "end": v(-13.21, 25.34) * mm});
            skLineSegment(sketch, "E30.0.91", {"start": v(-13.21, 25.34) * mm, "end": v(-13.47, 25.2) * mm});
            skLineSegment(sketch, "E30.0.92", {"start": v(-13.47, 25.2) * mm, "end": v(-13.73, 25.06) * mm});
            skArc(sketch, "E30.0.93", {"start": v(-13.73, 25.06) * mm, "mid": v(-14.23, 23.18) * mm, "end": v(-14.14, 21.24) * mm});
            skArc(sketch, "E30.0.94", {"start": v(-14.14, 21.24) * mm, "mid": v(-14.1, 21.13) * mm, "end": v(-14.06, 21.02) * mm});
            skLineSegment(sketch, "E30.0.95", {"start": v(-14.06, 21.02) * mm, "end": v(-12.93, 18.91) * mm});
            skArc(sketch, "E30.0.96", {"start": v(-12.93, 18.91) * mm, "mid": v(-12.86, 18.37) * mm, "end": v(-13.16, 17.9) * mm});
            skArc(sketch, "E30.0.97", {"start": v(-13.16, 17.9) * mm, "mid": v(-14.1, 17.18) * mm, "end": v(-15, 16.4) * mm});
            skArc(sketch, "E30.0.98", {"start": v(-15, 16.4) * mm, "mid": v(-15.5, 16.2) * mm, "end": v(-16.03, 16.37) * mm});
            skLineSegment(sketch, "E30.0.99", {"start": v(-16.03, 16.37) * mm, "end": v(-17.87, 17.9) * mm});
            skArc(sketch, "E30.0.100", {"start": v(-17.87, 17.9) * mm, "mid": v(-17.97, 17.96) * mm, "end": v(-18.07, 18) * mm});
            skArc(sketch, "E30.0.101", {"start": v(-18.07, 18) * mm, "mid": v(-19.96, 18.48) * mm, "end": v(-21.9, 18.35) * mm});
            skLineSegment(sketch, "E30.0.102", {"start": v(-21.9, 18.35) * mm, "end": v(-22.09, 18.13) * mm});
            skLineSegment(sketch, "E30.0.103", {"start": v(-22.09, 18.13) * mm, "end": v(-22.27, 17.9) * mm});
            skArc(sketch, "E30.0.104", {"start": v(-22.27, 17.9) * mm, "mid": v(-22.02, 15.97) * mm, "end": v(-21.19, 14.2) * mm});
            skArc(sketch, "E30.0.105", {"start": v(-21.19, 14.2) * mm, "mid": v(-21.12, 14.12) * mm, "end": v(-21.03, 14.04) * mm});
            skLineSegment(sketch, "E30.0.106", {"start": v(-21.03, 14.04) * mm, "end": v(-19.19, 12.53) * mm});
            skArc(sketch, "E30.0.107", {"start": v(-19.19, 12.53) * mm, "mid": v(-18.91, 12.05) * mm, "end": v(-19.01, 11.5) * mm});
            skArc(sketch, "E30.0.108", {"start": v(-19.01, 11.5) * mm, "mid": v(-19.6, 10.48) * mm, "end": v(-20.13, 9.41) * mm});
            skArc(sketch, "E30.0.109", {"start": v(-20.13, 9.41) * mm, "mid": v(-20.53, 9.03) * mm, "end": v(-21.07, 9) * mm});
            skLineSegment(sketch, "E30.0.110", {"start": v(-21.07, 9) * mm, "end": v(-23.36, 9.69) * mm});
            skArc(sketch, "E30.0.111", {"start": v(-23.36, 9.69) * mm, "mid": v(-23.47, 9.71) * mm, "end": v(-23.58, 9.72) * mm});
            skArc(sketch, "E30.0.112", {"start": v(-23.58, 9.72) * mm, "mid": v(-25.51, 9.43) * mm, "end": v(-27.26, 8.58) * mm});
            skLineSegment(sketch, "E30.0.113", {"start": v(-27.26, 8.58) * mm, "end": v(-27.35, 8.3) * mm});
            skLineSegment(sketch, "E30.0.114", {"start": v(-27.35, 8.3) * mm, "end": v(-27.43, 8.01) * mm});
            skArc(sketch, "E30.0.115", {"start": v(-27.43, 8.01) * mm, "mid": v(-26.45, 6.33) * mm, "end": v(-25.01, 5.02) * mm});
            skArc(sketch, "E30.0.116", {"start": v(-25.01, 5.02) * mm, "mid": v(-24.91, 4.96) * mm, "end": v(-24.8, 4.92) * mm});
            skLineSegment(sketch, "E30.0.117", {"start": v(-24.8, 4.92) * mm, "end": v(-22.52, 4.23) * mm});
            skArc(sketch, "E30.0.118", {"start": v(-22.52, 4.23) * mm, "mid": v(-22.08, 3.9) * mm, "end": v(-21.97, 3.36) * mm});
            skArc(sketch, "E30.0.119", {"start": v(-21.97, 3.36) * mm, "mid": v(-22.12, 2.18) * mm, "end": v(-22.2, 1) * mm});
            skArc(sketch, "E30.0.120", {"start": v(-22.2, 1) * mm, "mid": v(-22.42, 0.49) * mm, "end": v(-22.91, 0.25) * mm});
            skLineSegment(sketch, "E30.0.121", {"start": v(-22.91, 0.25) * mm, "end": v(-25.29, 0.01) * mm});
            skArc(sketch, "E30.0.122", {"start": v(-25.29, 0.01) * mm, "mid": v(-25.4, 0) * mm, "end": v(-25.51, -0.04) * mm});
            skArc(sketch, "E30.0.123", {"start": v(-25.51, -0.04) * mm, "mid": v(-27.18, -1.05) * mm, "end": v(-28.46, -2.5) * mm});
            skLineSegment(sketch, "E30.0.124", {"start": v(-28.46, -2.5) * mm, "end": v(-28.44, -2.8) * mm});
            skLineSegment(sketch, "E30.0.125", {"start": v(-28.44, -2.8) * mm, "end": v(-28.4, -3.1) * mm});
            skArc(sketch, "E30.0.126", {"start": v(-28.4, -3.1) * mm, "mid": v(-26.86, -4.28) * mm, "end": v(-25.03, -4.93) * mm});
            skArc(sketch, "E30.0.127", {"start": v(-25.03, -4.93) * mm, "mid": v(-24.92, -4.95) * mm, "end": v(-24.8, -4.94) * mm});
            skLineSegment(sketch, "E30.0.128", {"start": v(-24.8, -4.94) * mm, "end": v(-22.42, -4.71) * mm});
            skArc(sketch, "E30.0.129", {"start": v(-22.42, -4.71) * mm, "mid": v(-21.9, -4.85) * mm, "end": v(-21.58, -5.3) * mm});
            skArc(sketch, "E30.0.130", {"start": v(-21.58, -5.3) * mm, "mid": v(-21.27, -6.45) * mm, "end": v(-20.9, -7.58) * mm});
            skArc(sketch, "E30.0.131", {"start": v(-20.9, -7.58) * mm, "mid": v(-20.9, -8.13) * mm, "end": v(-21.26, -8.54) * mm});
            skLineSegment(sketch, "E30.0.132", {"start": v(-21.26, -8.54) * mm, "end": v(-23.37, -9.67) * mm});
            skArc(sketch, "E30.0.133", {"start": v(-23.37, -9.67) * mm, "mid": v(-23.47, -9.73) * mm, "end": v(-23.55, -9.8) * mm});
            skArc(sketch, "E30.0.134", {"start": v(-23.55, -9.8) * mm, "mid": v(-24.7, -11.37) * mm, "end": v(-25.34, -13.21) * mm});
            skLineSegment(sketch, "E30.0.135", {"start": v(-25.34, -13.21) * mm, "end": v(-25.2, -13.47) * mm});
            skLineSegment(sketch, "E30.0.136", {"start": v(-25.2, -13.47) * mm, "end": v(-25.06, -13.73) * mm});
            skArc(sketch, "E30.0.137", {"start": v(-25.06, -13.73) * mm, "mid": v(-23.18, -14.23) * mm, "end": v(-21.24, -14.14) * mm});
            skArc(sketch, "E30.0.138", {"start": v(-21.24, -14.14) * mm, "mid": v(-21.13, -14.1) * mm, "end": v(-21.02, -14.06) * mm});
            skLineSegment(sketch, "E30.0.139", {"start": v(-21.02, -14.06) * mm, "end": v(-18.91, -12.93) * mm});
            skArc(sketch, "E30.0.140", {"start": v(-18.91, -12.93) * mm, "mid": v(-18.37, -12.86) * mm, "end": v(-17.9, -13.16) * mm});
            skArc(sketch, "E30.0.141", {"start": v(-17.9, -13.16) * mm, "mid": v(-17.18, -14.1) * mm, "end": v(-16.4, -15) * mm});
            skArc(sketch, "E30.0.142", {"start": v(-16.4, -15) * mm, "mid": v(-16.2, -15.5) * mm, "end": v(-16.37, -16.03) * mm});
            skLineSegment(sketch, "E30.0.143", {"start": v(-16.37, -16.03) * mm, "end": v(-17.9, -17.87) * mm});
            skArc(sketch, "E30.0.144", {"start": v(-17.9, -17.87) * mm, "mid": v(-17.96, -17.97) * mm, "end": v(-18, -18.07) * mm});
            skArc(sketch, "E30.0.145", {"start": v(-18, -18.07) * mm, "mid": v(-18.48, -19.96) * mm, "end": v(-18.35, -21.9) * mm});
            skLineSegment(sketch, "E30.0.146", {"start": v(-18.35, -21.9) * mm, "end": v(-18.13, -22.09) * mm});
            skLineSegment(sketch, "E30.0.147", {"start": v(-18.13, -22.09) * mm, "end": v(-17.9, -22.27) * mm});
            skArc(sketch, "E30.0.148", {"start": v(-17.9, -22.27) * mm, "mid": v(-15.97, -22.02) * mm, "end": v(-14.2, -21.19) * mm});
            skArc(sketch, "E30.0.149", {"start": v(-14.2, -21.19) * mm, "mid": v(-14.12, -21.12) * mm, "end": v(-14.04, -21.03) * mm});
            skLineSegment(sketch, "E30.0.150", {"start": v(-14.04, -21.03) * mm, "end": v(-12.53, -19.19) * mm});
            skArc(sketch, "E30.0.151", {"start": v(-12.53, -19.19) * mm, "mid": v(-12.05, -18.91) * mm, "end": v(-11.5, -19.01) * mm});
            skArc(sketch, "E30.0.152", {"start": v(-11.5, -19.01) * mm, "mid": v(-10.48, -19.6) * mm, "end": v(-9.41, -20.13) * mm});
            skArc(sketch, "E30.0.153", {"start": v(-9.41, -20.13) * mm, "mid": v(-9.03, -20.53) * mm, "end": v(-9, -21.07) * mm});
            skLineSegment(sketch, "E30.0.154", {"start": v(-9, -21.07) * mm, "end": v(-9.69, -23.36) * mm});
            skArc(sketch, "E30.0.155", {"start": v(-9.69, -23.36) * mm, "mid": v(-9.71, -23.47) * mm, "end": v(-9.72, -23.58) * mm});
            skArc(sketch, "E30.0.156", {"start": v(-9.72, -23.58) * mm, "mid": v(-9.43, -25.51) * mm, "end": v(-8.58, -27.26) * mm});
            skLineSegment(sketch, "E30.0.157", {"start": v(-8.58, -27.26) * mm, "end": v(-8.3, -27.35) * mm});
            skLineSegment(sketch, "E30.0.158", {"start": v(-8.3, -27.35) * mm, "end": v(-8.01, -27.43) * mm});
            skArc(sketch, "E30.0.159", {"start": v(-8.01, -27.43) * mm, "mid": v(-6.33, -26.45) * mm, "end": v(-5.02, -25.01) * mm});
            skArc(sketch, "E30.0.160", {"start": v(-5.02, -25.01) * mm, "mid": v(-4.96, -24.91) * mm, "end": v(-4.92, -24.8) * mm});
            skLineSegment(sketch, "E30.0.161", {"start": v(-4.92, -24.8) * mm, "end": v(-4.23, -22.52) * mm});
            skArc(sketch, "E30.0.162", {"start": v(-4.23, -22.52) * mm, "mid": v(-3.9, -22.08) * mm, "end": v(-3.36, -21.97) * mm});
            skArc(sketch, "E30.0.163", {"start": v(-3.36, -21.97) * mm, "mid": v(-2.18, -22.12) * mm, "end": v(-1, -22.2) * mm});
            skArc(sketch, "E30.0.164", {"start": v(-1, -22.2) * mm, "mid": v(-0.49, -22.42) * mm, "end": v(-0.25, -22.91) * mm});
            skLineSegment(sketch, "E30.0.165", {"start": v(-0.25, -22.91) * mm, "end": v(-0.01, -25.29) * mm});
            skArc(sketch, "E30.0.166", {"start": v(-0.01, -25.29) * mm, "mid": v(0, -25.4) * mm, "end": v(0.04, -25.51) * mm});
            skArc(sketch, "E30.0.167", {"start": v(0.04, -25.51) * mm, "mid": v(1.05, -27.18) * mm, "end": v(2.5, -28.46) * mm});
            skLineSegment(sketch, "E30.0.168", {"start": v(2.5, -28.46) * mm, "end": v(2.8, -28.44) * mm});
            skLineSegment(sketch, "E30.0.169", {"start": v(2.8, -28.44) * mm, "end": v(3.1, -28.4) * mm});
            skArc(sketch, "E30.0.170", {"start": v(3.1, -28.4) * mm, "mid": v(4.28, -26.86) * mm, "end": v(4.93, -25.03) * mm});
            skArc(sketch, "E30.0.171", {"start": v(4.93, -25.03) * mm, "mid": v(4.95, -24.92) * mm, "end": v(4.94, -24.8) * mm});
            skLineSegment(sketch, "E30.0.172", {"start": v(4.94, -24.8) * mm, "end": v(4.71, -22.42) * mm});
            skArc(sketch, "E30.0.173", {"start": v(4.71, -22.42) * mm, "mid": v(4.85, -21.9) * mm, "end": v(5.3, -21.58) * mm});
            skArc(sketch, "E30.0.174", {"start": v(5.3, -21.58) * mm, "mid": v(6.45, -21.27) * mm, "end": v(7.58, -20.9) * mm});
            skArc(sketch, "E30.0.175", {"start": v(7.58, -20.9) * mm, "mid": v(8.13, -20.9) * mm, "end": v(8.54, -21.26) * mm});
            skSolve(sketch);
        }
        {
            var Q0;
            Q0=makeQuery(id+"F2.imprint","IMPRINT",FACE,{"disambiguationData":[TD([[makeQuery(id+"F2.imprint","IMPRINT",EDGE,{"derivedFrom":sQuery(id+"F2.wireOp",EDGE,"E30.0.0")}),1.0]])]});
            var Q1;
            Q1=makeQuery(id+"F0.imprint","IMPRINT",FACE,{"disambiguationData":[TD([[makeQuery(id+"F0.imprint","IMPRINT",EDGE,{"derivedFrom":sQuery(id+"F0.wireOp",EDGE,"E0")}),1.0]])]});
            var Q2;
            Q2=sQuery(id+"F2.wireOp",VERTEX,"E30.0.94.end");
            var Q3;
            Q3=sQuery(id+"F0.wireOp",VERTEX,"E6.MirrorCS.start");
            loft(context, id + "F3", {"sheetProfilesArray" : [{ "sheetProfileEntities" : qUnion([Q0]) }, { "sheetProfileEntities" : qUnion([Q1]) }], "matchConnections" : true, "connections" : [{ "connectionEntities" : qUnion([Q2, Q3]), "connectionEdgeQueries" : qUnion([]), "connectionEdgeParameters" : [] }]});
        }
        {
            var Q0;
            Q0=makeQuery(id+"F3.opLoft","CAP_FACE",FACE,{"disambiguationData":[OSD([makeQuery(id+"F2.imprint","IMPRINT",FACE,{"disambiguationData":[TD([[makeQuery(id+"F2.imprint","IMPRINT",EDGE,{"derivedFrom":sQuery(id+"F2.wireOp",EDGE,"E30.0.0")}),1.0]])]})])],"isStart":true});
            var sketch = newSketch(context, id + "F4", { "sketchPlane" : qUnion([Q0])});
            skCircle(sketch, "E31", {"center": v(0, 0) * mm, "radius": 6.35 * mm});
            skSolve(sketch);
        }
        {
            var Q0;
            Q0=makeQuery(id+"F4.imprint","IMPRINT",FACE,{"disambiguationData":[TD([[makeQuery(id+"F4.imprint","IMPRINT",EDGE,{"derivedFrom":sQuery(id+"F4.wireOp",EDGE,"E31")}),1.0]])]});
            extrude(context, id + "F5", {"entities" : qUnion([Q0]), "operationType" : NewBodyOperationType.REMOVE, "oppositeDirection" : true, "depth" : 50.8 * mm});
        }
    });
